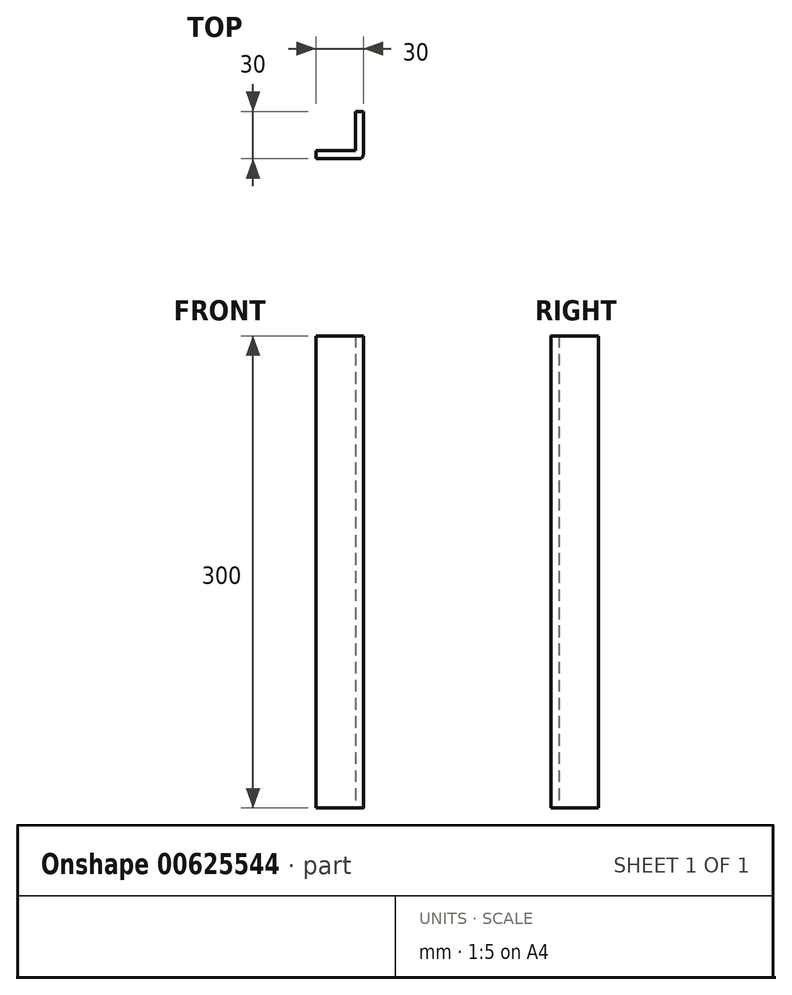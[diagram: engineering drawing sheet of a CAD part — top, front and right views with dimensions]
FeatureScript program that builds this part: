
annotation { "Feature Type Name" : "Feature", "Feature Type Description" : "" }
export const myFeature = defineFeature(function(context is Context, id is Id, definition is map)
    precondition{}
    {
        {
            var Q0;
            Q0=qCreatedBy(makeId("Top.planeOp"),FACE);
            var sketch = newSketch(context, id + "F0", { "sketchPlane" : qUnion([Q0])});
            skLineSegment(sketch, "E0.bottom", {"start": v(10, 15) * mm, "end": v(15, 15) * mm});
            skLineSegment(sketch, "E0.top", {"start": v(-15, -15) * mm, "end": v(12.5, -15) * mm});
            skLineSegment(sketch, "E0.left", {"start": v(-15, -10) * mm, "end": v(-15, -15) * mm});
            skLineSegment(sketch, "E0.right", {"start": v(15, 15) * mm, "end": v(15, -12.5) * mm});
            skPoint(sketch, "E0.middle", {"position": v(0, 0) * mm});
            skLineSegment(sketch, "E1", {"start": v(-15, -10) * mm, "end": v(10, -10) * mm});
            skLineSegment(sketch, "E2", {"start": v(10, -10) * mm, "end": v(10, 15) * mm});
            skPoint(sketch, "E3.orphan", {"position": v(-15, 15) * mm});
            skPoint(sketch, "E4.visualSharp", {"position": v(10, -10) * mm});
            skLineSegment(sketch, "E4.filletArc", {"start": v(10, -10) * mm, "end": v(10, -10) * mm});
            skPoint(sketch, "E5.visualSharp", {"position": v(15, -15) * mm});
            skArc(sketch, "E5.filletArc", {"start": v(12.5, -15) * mm, "mid": v(14.27, -14.27) * mm, "end": v(15, -12.5) * mm});
            skSolve(sketch);
        }
        {
            var Q0;
            Q0 = qSketchRegion(id + "F0", true);
            extrude(context, id + "F1", {"entities" : qUnion([Q0]), "depth" : 300 * mm, "offsetDistance" : 25 * mm});
        }
    });
